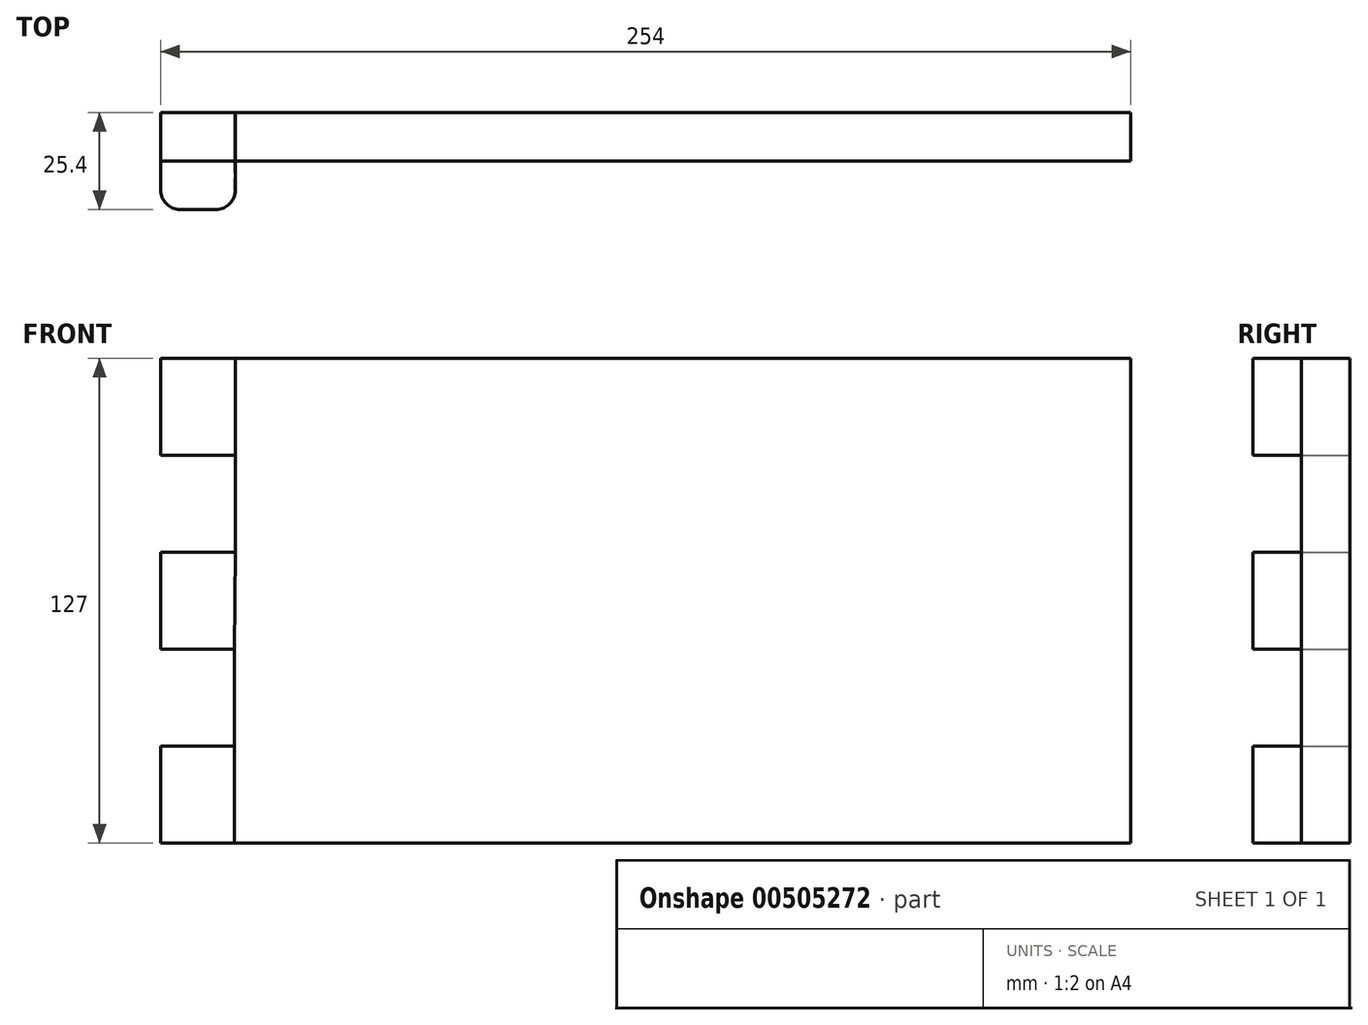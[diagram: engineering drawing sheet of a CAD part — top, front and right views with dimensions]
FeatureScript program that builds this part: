
annotation { "Feature Type Name" : "Feature", "Feature Type Description" : "" }
export const myFeature = defineFeature(function(context is Context, id is Id, definition is map)
    precondition{}
    {
        {
            var Q0;
            Q0=qCreatedBy(makeId("Front.planeOp"),FACE);
            var sketch = newSketch(context, id + "F0", { "sketchPlane" : qUnion([Q0])});
            skLineSegment(sketch, "E0.bottom", {"start": v(-127, 63.5) * mm, "end": v(127, 63.5) * mm});
            skLineSegment(sketch, "E0.top", {"start": v(-127, -63.5) * mm, "end": v(127, -63.5) * mm});
            skLineSegment(sketch, "E0.left", {"start": v(-127, 63.5) * mm, "end": v(-127, 38.1) * mm});
            skLineSegment(sketch, "E0.right", {"start": v(127, 63.5) * mm, "end": v(127, -63.5) * mm});
            skPoint(sketch, "E0.middle", {"position": v(0, 0) * mm});
            skLineSegment(sketch, "E1", {"start": v(-127, 38.1) * mm, "end": v(-107.44, 38.1) * mm});
            skLineSegment(sketch, "E2", {"start": v(-107.44, 38.1) * mm, "end": v(-107.44, 12.7) * mm});
            skLineSegment(sketch, "E3", {"start": v(-107.44, 12.7) * mm, "end": v(-127, 12.7) * mm});
            skLineSegment(sketch, "E4", {"start": v(-127, -12.7) * mm, "end": v(-107.65, -12.7) * mm});
            skLineSegment(sketch, "E5", {"start": v(-107.65, -12.7) * mm, "end": v(-107.65, -38.1) * mm});
            skLineSegment(sketch, "E6", {"start": v(-107.65, -38.1) * mm, "end": v(-127, -38.1) * mm});
            skLineSegment(sketch, "E7.trimOffspring", {"start": v(-127, 12.7) * mm, "end": v(-127, -12.7) * mm});
            skLineSegment(sketch, "E8.trimOffspring", {"start": v(-127, -38.1) * mm, "end": v(-127, -63.5) * mm});
            skPoint(sketch, "E9.trimOffspring.start.orphan", {"position": v(-127, -59.82) * mm});
            skLineSegment(sketch, "E10", {"start": v(-107.44, 38.1) * mm, "end": v(-107.44, 63.5) * mm});
            skLineSegment(sketch, "E11", {"start": v(-107.44, 12.7) * mm, "end": v(-107.65, -12.7) * mm});
            skLineSegment(sketch, "E12", {"start": v(-107.65, -38.1) * mm, "end": v(-107.65, -63.5) * mm});
            skSolve(sketch);
        }
        {
            var Q0;
            {var subQ0=sQuery(id+"F0.wireOp",EDGE,"E0.left");Q0=makeQuery(id+"F0.imprint","IMPRINT",FACE,{"disambiguationData":[TD([[makeQuery(id+"F0.imprint","IMPRINT",EDGE,{"derivedFrom":subQ0}),1.0]])]});}
            var Q1;
            Q1=makeQuery(id+"F0.imprint","IMPRINT",FACE,{"disambiguationData":[TD([[makeQuery(id+"F0.imprint","IMPRINT",EDGE,{"derivedFrom":sQuery(id+"F0.wireOp",EDGE,"E3")}),1.0]])]});
            var Q2;
            Q2=makeQuery(id+"F0.imprint","IMPRINT",FACE,{"disambiguationData":[TD([[makeQuery(id+"F0.imprint","IMPRINT",EDGE,{"derivedFrom":sQuery(id+"F0.wireOp",EDGE,"E6")}),1.0]])]});
            extrude(context, id + "F1", {"entities" : qUnion([Q0, Q1, Q2]), "depth" : 25.4 * mm});
        }
        {
            var Q0;
            Q0 = qSketchRegion(id + "F0", true);
            extrude(context, id + "F2", {"entities" : qUnion([Q0]), "depth" : 12.7 * mm});
        }
        {
            var Q0;
            Q0=makeQuery(id+"F1.opExtrude","CAP_EDGE",EDGE,{"disambiguationData":[OSD([sQuery(id+"F0.wireOp",EDGE,"E10")])],"isStart":false});
            var Q1;
            Q1=makeQuery(id+"F1.opExtrude","CAP_EDGE",EDGE,{"disambiguationData":[OSD([sQuery(id+"F0.wireOp",EDGE,"E11")])],"isStart":false});
            var Q2;
            Q2=makeQuery(id+"F1.opExtrude","CAP_EDGE",EDGE,{"disambiguationData":[OSD([sQuery(id+"F0.wireOp",EDGE,"E12")])],"isStart":false});
            var Q3;
            Q3=makeQuery(id+"F1.opExtrude","CAP_EDGE",EDGE,{"disambiguationData":[OSD([sQuery(id+"F0.wireOp",EDGE,"E8.trimOffspring")])],"isStart":false});
            var Q4;
            Q4=makeQuery(id+"F1.opExtrude","CAP_EDGE",EDGE,{"disambiguationData":[OSD([sQuery(id+"F0.wireOp",EDGE,"E7.trimOffspring")])],"isStart":false});
            var Q5;
            Q5=makeQuery(id+"F1.opExtrude","CAP_EDGE",EDGE,{"disambiguationData":[OSD([sQuery(id+"F0.wireOp",EDGE,"E0.left")])],"isStart":false});
            fillet(context, id + "F3", {"entities" : qUnion([Q0, Q1, Q2, Q3, Q4, Q5]), "radius" : 5.08 * mm, "tangentPropagation" : true, "allowEdgeOverflow" : false});
        }
    });
